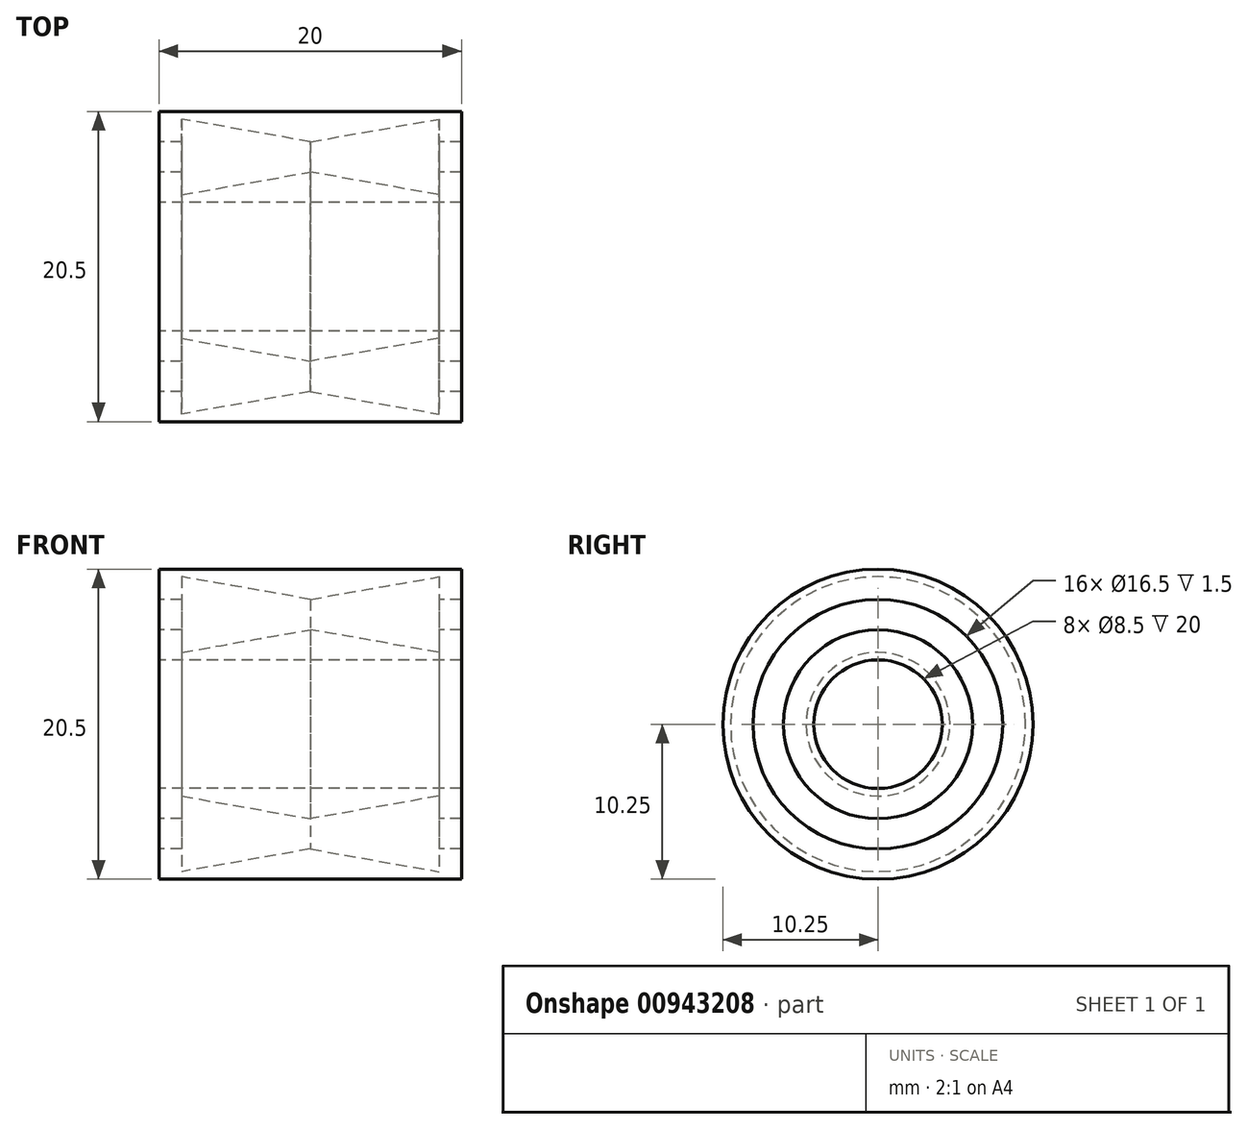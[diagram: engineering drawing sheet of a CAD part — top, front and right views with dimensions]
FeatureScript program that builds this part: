
annotation { "Feature Type Name" : "Feature", "Feature Type Description" : "" }
export const myFeature = defineFeature(function(context is Context, id is Id, definition is map)
    precondition{}
    {
        {
            var Q0;
            Q0=qCreatedBy(makeId("Top.planeOp"),FACE);
            var sketch = newSketch(context, id + "F0", { "sketchPlane" : qUnion([Q0])});
            skLineSegment(sketch, "E0", {"start": v(-10, 4.25) * mm, "end": v(10, 4.25) * mm});
            skLineSegment(sketch, "E1", {"start": v(10, 4.25) * mm, "end": v(10, 6.25) * mm});
            skLineSegment(sketch, "E2", {"start": v(10, 6.25) * mm, "end": v(8.5, 6.25) * mm});
            skLineSegment(sketch, "E3", {"start": v(8.5, 6.25) * mm, "end": v(8.5, 4.75) * mm});
            skLineSegment(sketch, "E4", {"start": v(8.5, 4.75) * mm, "end": v(0, 6.25) * mm});
            skLineSegment(sketch, "E5", {"start": v(0, 6.25) * mm, "end": v(-8.5, 4.75) * mm});
            skLineSegment(sketch, "E6", {"start": v(-8.5, 4.75) * mm, "end": v(-8.5, 6.25) * mm});
            skLineSegment(sketch, "E7", {"start": v(-8.5, 6.25) * mm, "end": v(-10, 6.25) * mm});
            skLineSegment(sketch, "E8", {"start": v(-10, 6.25) * mm, "end": v(-10, 4.25) * mm});
            skLineSegment(sketch, "E9", {"start": v(-10, 8.25) * mm, "end": v(-8.5, 8.25) * mm});
            skLineSegment(sketch, "E10", {"start": v(-8.5, 8.25) * mm, "end": v(-8.5, 9.75) * mm});
            skLineSegment(sketch, "E11", {"start": v(-8.5, 9.75) * mm, "end": v(0, 8.25) * mm});
            skLineSegment(sketch, "E12", {"start": v(0, 8.25) * mm, "end": v(8.5, 9.75) * mm});
            skLineSegment(sketch, "E13", {"start": v(10, 10.25) * mm, "end": v(-10, 10.25) * mm});
            skLineSegment(sketch, "E14", {"start": v(-10, 10.25) * mm, "end": v(-10, 8.25) * mm});
            skLineSegment(sketch, "E15", {"start": v(8.5, 9.75) * mm, "end": v(8.5, 8.25) * mm});
            skLineSegment(sketch, "E16", {"start": v(8.5, 8.25) * mm, "end": v(10, 8.25) * mm});
            skLineSegment(sketch, "E17", {"start": v(10, 10.25) * mm, "end": v(10, 8.25) * mm});
            skLineSegment(sketch, "E18", {"start": v(-16.97, 0) * mm, "end": v(29.93, 0) * mm});
            skSolve(sketch);
        }
        {
            var Q0;
            Q0=qSketchRegion(id+"F0",true);
            var Q1;
            Q1=sQuery(id+"F0.wireOp",EDGE,"E18");
            revolve(context, id + "F1", {"surfaceOperationType" : NewSurfaceOperationType.NEW, "entities" : qUnion([Q0]), "axis" : qUnion([Q1]), "revolveType" : RevolveType.FULL});
        }
    });
